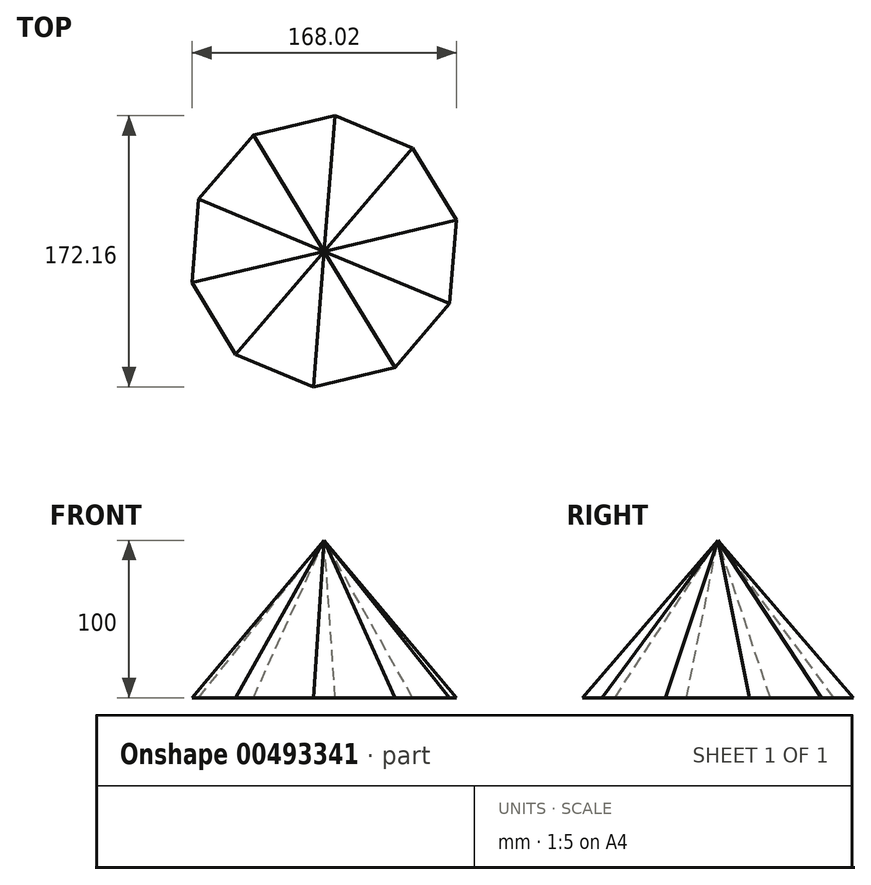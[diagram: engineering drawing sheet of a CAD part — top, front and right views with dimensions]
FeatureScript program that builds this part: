
annotation { "Feature Type Name" : "Feature", "Feature Type Description" : "" }
export const myFeature = defineFeature(function(context is Context, id is Id, definition is map)
    precondition{}
    {
        {
            var Q0;
            Q0=qCreatedBy(makeId("Top.planeOp"),FACE);
            var sketch = newSketch(context, id + "F0", { "sketchPlane" : qUnion([Q0])});
            skCircle(sketch, "E0.cCircle", {"center": v(0, 0) * mm, "radius": 86.35 * mm, "construction": true});
            skLineSegment(sketch, "E0.0", {"start": v(-79.72, 33.2) * mm, "end": v(-44.97, 73.72) * mm});
            skLineSegment(sketch, "E0.1", {"start": v(-44.97, 73.72) * mm, "end": v(6.95, 86.08) * mm});
            skLineSegment(sketch, "E0.2", {"start": v(6.95, 86.08) * mm, "end": v(56.21, 65.55) * mm});
            skLineSegment(sketch, "E0.3", {"start": v(56.21, 65.55) * mm, "end": v(84, 20) * mm});
            skLineSegment(sketch, "E0.4", {"start": v(84, 20) * mm, "end": v(79.72, -33.2) * mm});
            skLineSegment(sketch, "E0.5", {"start": v(79.72, -33.2) * mm, "end": v(44.97, -73.72) * mm});
            skLineSegment(sketch, "E0.6", {"start": v(44.97, -73.72) * mm, "end": v(-6.95, -86.08) * mm});
            skLineSegment(sketch, "E0.7", {"start": v(-6.95, -86.08) * mm, "end": v(-56.21, -65.55) * mm});
            skLineSegment(sketch, "E0.8", {"start": v(-56.21, -65.55) * mm, "end": v(-84, -20) * mm});
            skLineSegment(sketch, "E0.9", {"start": v(-84, -20) * mm, "end": v(-79.72, 33.2) * mm});
            skSolve(sketch);
        }
        {
            var Q0;
            Q0=qCreatedBy(makeId("Top.planeOp"),FACE);
            cPlane(context, id + "F1", {"entities" : qUnion([Q0]), "cplaneType" : CPlaneType.OFFSET, "offset" : 100 * mm, "width" : 150 * mm, "height" : 150 * mm});
        }
        {
            var Q0;
            Q0=qCreatedBy(id+"F1.planeOp",FACE);
            var sketch = newSketch(context, id + "F2", { "sketchPlane" : qUnion([Q0])});
            skPoint(sketch, "E1", {"position": v(0, 0) * mm});
            skSolve(sketch);
        }
        {
            var Q0;
            Q0=makeQuery(id+"F0.imprint","IMPRINT",FACE,{"disambiguationData":[TD([[makeQuery(id+"F0.imprint","IMPRINT",EDGE,{"derivedFrom":sQuery(id+"F0.wireOp",EDGE,"E0.0")}),-1.0]])]});
            var Q1;
            Q1=sQuery(id+"F2.wireOp",VERTEX,"E1");
            loft(context, id + "F3", {"sheetProfilesArray" : [{ "sheetProfileEntities" : qUnion([Q0]) }, { "sheetProfileEntities" : qUnion([Q1]) }]});
        }
    });
